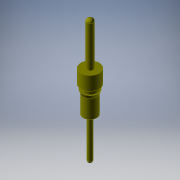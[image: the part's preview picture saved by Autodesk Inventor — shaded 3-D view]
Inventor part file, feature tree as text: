
AUTODESK INVENTOR PART (.ipt)
format: ipt  version: 2019 (Build 230136000, 136)  size: 145,920 bytes
history: native  units: in
note: dims shown in document units (in); Inventor stores cm internally (conversion verified against a paired STEP export)
features: other x7, revolve x3, sketch x3
ambient origin geometry x8: Origin, YZ Plane, XZ Plane, XY Plane, X Axis, Y Axis, Z Axis, Center Point
bodies: Solid1 (feature_tree)
feature tree (13):
  revolve  "Revolution1"  Angle=360.0deg
  revolve  "Revolution2"  [1 undecoded]
  revolve  "Revolution3"  [1 undecoded]
  other  "pins_XY"
  other  "pins_YZ"
  other  "pins_ZX"
  other  "pins_X"
  other  "pins_Y"
  other  "pins_Z"
  other  "pins_Center"
  sketch  "Sketch_1"  dims[d0=360.0deg d1=360.0deg]
  sketch  "Sketch_3"  dims[d2=360.0deg d3=0.0in]
  sketch  "Sketch_14"
note: 2 required parameter values undecoded (feature->parameter linkage not recoverable at this tier; creation-order binding heuristic only, values carry confidence <= 0.55)